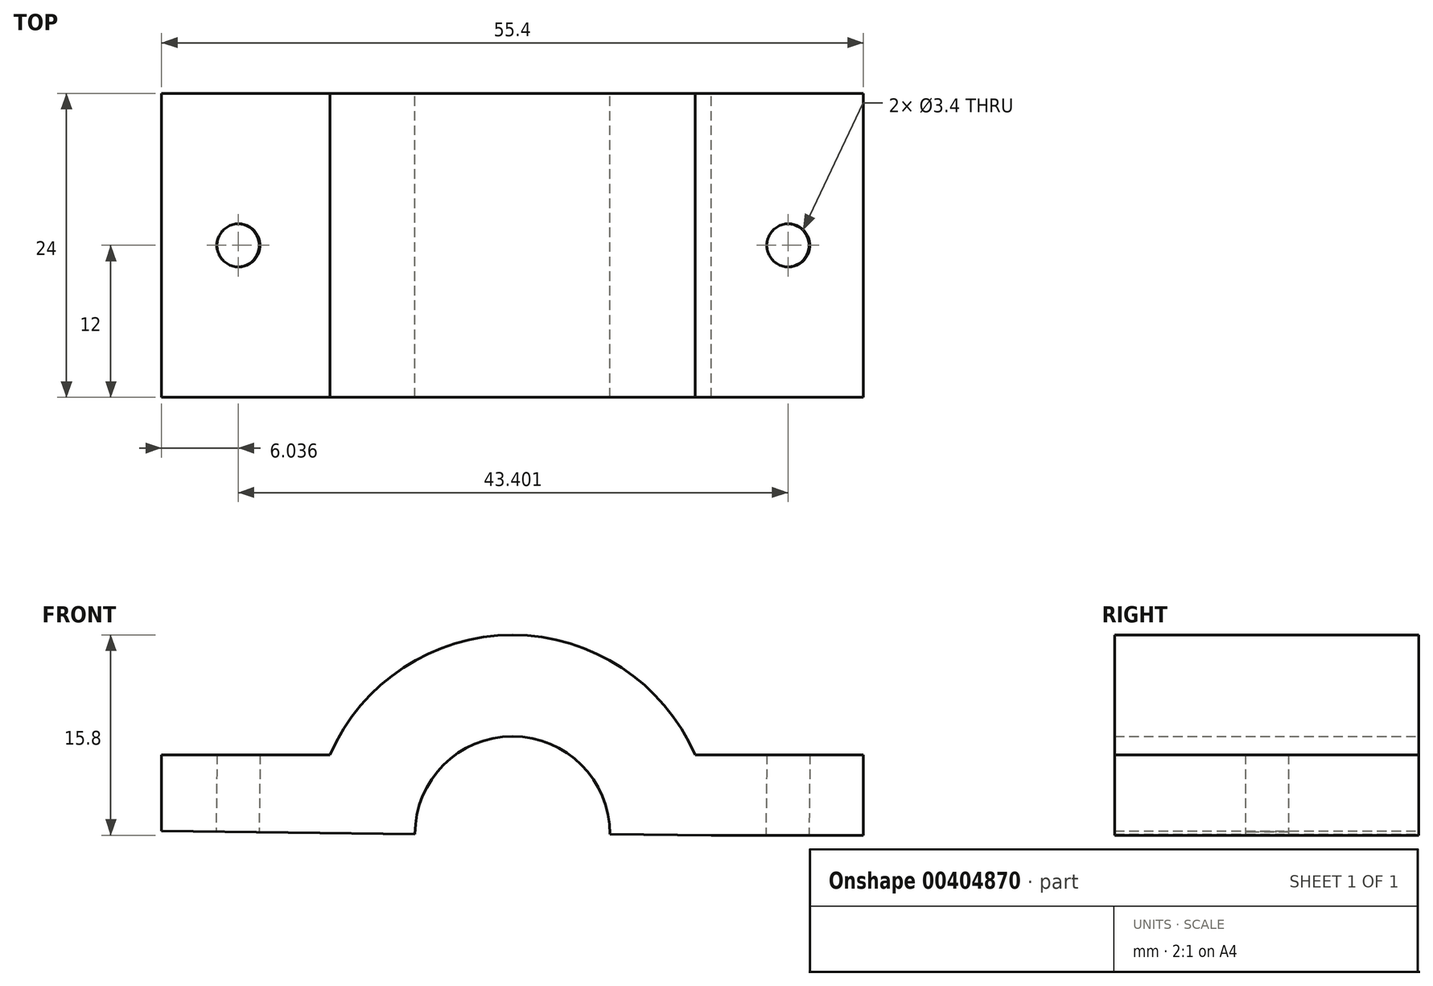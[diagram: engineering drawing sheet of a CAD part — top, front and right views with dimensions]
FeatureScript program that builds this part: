
annotation { "Feature Type Name" : "Feature", "Feature Type Description" : "" }
export const myFeature = defineFeature(function(context is Context, id is Id, definition is map)
    precondition{}
    {
        {
            var Q0;
            Q0=qCreatedBy(makeId("Front.planeOp"),FACE);
            var sketch = newSketch(context, id + "F0", { "sketchPlane" : qUnion([Q0])});
            skArc(sketch, "E0", {"start": v(7.7, -0.17) * mm, "mid": v(0, 7.53) * mm, "end": v(-7.7, -0.17) * mm});
            skArc(sketch, "E1", {"start": v(14.4, 6.07) * mm, "mid": v(0, 15.53) * mm, "end": v(-14.4, 6.07) * mm});
            skLineSegment(sketch, "E2", {"start": v(-7.7, -0.17) * mm, "end": v(-15.7, -0.07) * mm});
            skLineSegment(sketch, "E3", {"start": v(7.7, -0.17) * mm, "end": v(15.7, -0.27) * mm});
            skLineSegment(sketch, "E4", {"start": v(15.7, -0.27) * mm, "end": v(27.7, -0.27) * mm});
            skLineSegment(sketch, "E5", {"start": v(-15.7, -0.07) * mm, "end": v(-27.7, 0.07) * mm});
            skLineSegment(sketch, "E6", {"start": v(-27.7, 0.07) * mm, "end": v(-27.7, 6.07) * mm});
            skLineSegment(sketch, "E7", {"start": v(27.7, -0.27) * mm, "end": v(27.7, 6.07) * mm});
            skLineSegment(sketch, "E8", {"start": v(-27.7, 6.07) * mm, "end": v(-14.4, 6.07) * mm});
            skLineSegment(sketch, "E9", {"start": v(27.7, 6.07) * mm, "end": v(14.4, 6.07) * mm});
            skSolve(sketch);
        }
        {
            var Q0;
            Q0=makeQuery(id+"F0.imprint","IMPRINT",FACE,{"disambiguationData":[TD([[makeQuery(id+"F0.imprint","IMPRINT",EDGE,{"derivedFrom":sQuery(id+"F0.wireOp",EDGE,"E0")}),-1.0]])]});
            extrude(context, id + "F1", {"entities" : qUnion([Q0]), "depth" : 24 * mm});
        }
        {
            var Q0;
            Q0=makeQuery(id+"F1.opExtrude","SWEPT_FACE",FACE,{"disambiguationData":[OSD([sQuery(id+"F0.wireOp",EDGE,"E2"),sQuery(id+"F0.wireOp",EDGE,"E5")])]});
            var sketch = newSketch(context, id + "F2", { "sketchPlane" : qUnion([Q0])});
            skLineSegment(sketch, "E10", {"start": v(0, 12) * mm, "end": v(-21.7, 12) * mm, "construction": true});
            skPoint(sketch, "E10.startSnap0", {"position": v(-27.7, 12) * mm});
            skPoint(sketch, "E10.endSnap0", {"position": v(-7.7, 12) * mm});
            skLineSegment(sketch, "E11", {"start": v(0, 12) * mm, "end": v(21.7, 12) * mm, "construction": true});
            skCircle(sketch, "E12", {"center": v(-21.7, 12) * mm, "radius": 1.7 * mm});
            skCircle(sketch, "E13", {"center": v(21.7, 12) * mm, "radius": 1.7 * mm});
            skSolve(sketch);
        }
        {
            var Q0;
            Q0=makeQuery(id+"F2.imprint","IMPRINT",FACE,{"disambiguationData":[TD([[makeQuery(id+"F2.imprint","IMPRINT",EDGE,{"derivedFrom":sQuery(id+"F2.wireOp",EDGE,"E12")}),1.0]])]});
            var Q1;
            Q1=makeQuery(id+"F2.imprint","IMPRINT",FACE,{"disambiguationData":[TD([[makeQuery(id+"F2.imprint","IMPRINT",EDGE,{"derivedFrom":sQuery(id+"F2.wireOp",EDGE,"E13")}),1.0]])]});
            extrude(context, id + "F3", {"entities" : qUnion([Q0, Q1]), "operationType" : NewBodyOperationType.REMOVE, "oppositeDirection" : true, "depth" : 25 * mm});
        }
    });
